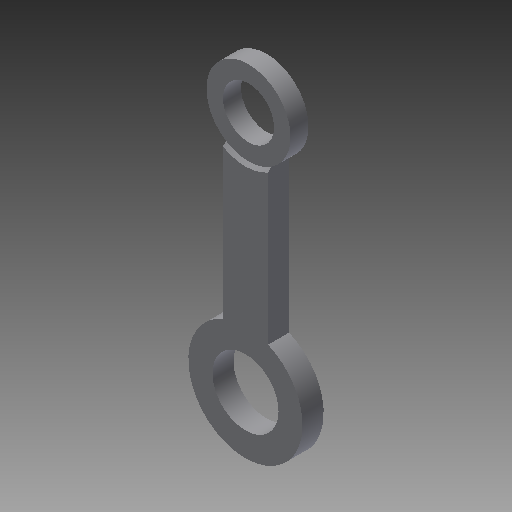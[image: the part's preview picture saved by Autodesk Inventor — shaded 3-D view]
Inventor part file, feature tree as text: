
AUTODESK INVENTOR PART (.ipt)
format: ipt  version: 2017 SP1 (Build 210196100, 196)  size: 121,344 bytes
history: native  units: mm
features: extrude x2, sketch x2, chamfer x1
ambient origin geometry x8: Origin, YZ Plane, XZ Plane, XY Plane, X Axis, Y Axis, Z Axis, Center Point
bodies: Solid1 (feature_tree)
feature tree (5):
  extrude  "Extrusion1"  Depth=17.0mm
  extrude  "Extrusion2"  Depth=80.0mm
  chamfer  "Chamfer1"  Distance=8.0mm
  sketch  "Sketch1"  dims[d0=22.0mm d1=17.0mm]
  sketch  "Sketch2"  dims[d2=80.0mm d3=5.5mm d4=8.0mm d5=15.0mm d6=7.0mm d7=0.0mm d8=1.0mm d9=0.0mm d10=1.0mm d11=2.0mm d12=45.0deg]
